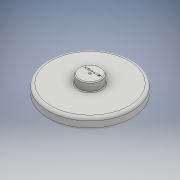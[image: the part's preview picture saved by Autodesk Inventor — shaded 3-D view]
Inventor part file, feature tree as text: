
AUTODESK INVENTOR PART (.ipt)
format: ipt  version: 2018 (Build 220112000, 112)  size: 169,472 bytes
history: native  units: mm
features: sketch x8, fillet x4, extrude x3, other x1, hole x1
ambient origin geometry x8: Origin, YZ Plane, XZ Plane, XY Plane, X Axis, Y Axis, Z Axis, Center Point
bodies: Body1 (feature_tree)
feature tree (17):
  other  "ソリッド1"
  extrude  "押し出し1"  Depth=490.0mm
  fillet  "フィレット1"  Radius=70.0mm
  sketch  "スケッチ4"
  extrude  "押し出し2"  Depth=17.5mm
  extrude  "押し出し3"  Depth=128.0mm
  fillet  "フィレット2"  Radius=50.0mm
  fillet  "フィレット3"  Radius=216.0mm
  fillet  "フィレット4"  Radius=48.0mm
  hole  "穴2"  [1 undecoded]
  sketch  "スケッチ12"
  sketch  "スケッチ13"
  sketch  "スケッチ14"
  sketch  "スケッチ1"
  sketch  "スケッチ8"
  sketch  "スケッチ9"
  sketch  "スケッチ10"
note: 1 required parameter value undecoded (feature->parameter linkage not recoverable at this tier; creation-order binding heuristic only, values carry confidence <= 0.55)
